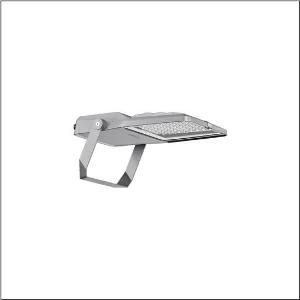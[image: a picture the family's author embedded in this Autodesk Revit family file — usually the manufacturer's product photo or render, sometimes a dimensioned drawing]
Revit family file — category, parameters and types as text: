
# Revit family: floodlight_fl_21_iq_mini___pl64_5xa7771c4e1a_d4bc
name_source: partatom
category: Lighting Fixtures
units: mm (PartAtom-declared; Revit-internal decimal feet)

## family parameters
Cut with Voids When Loaded = No
Host = Face
Light Source = No
Part Type = Normal
Room Calculation Point = No
Round Connector Dimension = Use Diameter
Shared = No

## types (1)
- --- (1 x LED, 12280 lm, 87.2 W, 4000K)
    Apparent Load = 87 VA
    CIE Flux Codes = 28 80 98 100 100
    Color Rendering = 70
    Color Temperature = 4000K
    Default Elevation = 1800 mm
    Description = Floodlight FL 21 iQ mini, floodlight, primary light control with lens, of PMMA, primary optical cover: protective disc, of toughened safety glass, transparent, light distribution: PL64, light emission: direct distribution, installation type: surface-mounted, lamps: LED, High Power LED, rated values: 12.280lm | 87,2W | 140,8lm/W (begin service life); end service life: 12.280lm | 92,1W; at 50% lumin. flux: 6.140lm | 40,2W | 152,7lm/W, colour temperature: 4000K, colour rendering: CRI > 70, light colour: 740, light setting 1 begin service life: 100% | 12.280lm | 87,2W | 140,8lm/W | 4.000K, light setting 1 end service life: 92,1W, further light settings possible, control: Auto-Match, Temp-Guard, Lumen-Switch, Night-Set, Smart-Wire, Light-Fading, Desk-Remote (wireless, voltage-free reading and setting of iQ features in the workshop via application-optimized NFC function/RFID function), optimised constant luminous flux control (CLO 2.0), pre-setting: linear dimming characteristic, with terminal, 6-pole, mains connection: 220..240V, AC, 50/60Hz, luminaire housing, of diecast aluminium, powder-coated, SITECO metallic grey (DB 702S), corrosivity category C5 mid according to DIN EN ISO 12944suitable for swimming poolschlorine-resistant, sealing non-destructively replaceable, mounting bracket, of steel, galvanised, powder-coated, SITECO metallic grey (DB 702S), protection rating (complete): IP66, insulation class (complete): insulation class II (safety insulation), certification: CE, ENEC, VDE, protection symbol: D, impact resistance: IK08, permissible operating ambient temperature: -40..+40°C, permissible operating ambient temperature for outdoor applications: -40..+50°C, standard: DIN EN 12944, LABS conformity tested according to VDMA 24364:2018-05, packaging unit: 1 piece

Light Distribution: PL64
    Height = 70 mm
    Lamp = 1 x LED
    Lamp Light Flux = 12280 lm
    Lamp Power = 87.2 W
    Lamp count = 1
    Length = 485 mm
    Luminous efficacy = 141 lm/W
    Manufacturer = Siteco
    ModVariant = No
    Model = 5XA7771C4E1A
    Mounting Place = Pole
    Mounting Type = Pole annexe
    Number of Poles = 1
    OnlyDefault = Yes
    Power Factor = 1
    Product Name = Floodlight FL 21 iQ mini | PL64
    Product group = floodlight | pylon annexe
    ProductGroupID = 6201
    Protection Class = Protection class II
    Protection Degree = IP 66
    RLX_Detail_Level = 1
    RLX_Emergency_Light_Flux = 0 lm
    RLX_Emergency_Type = 0
    RLX_Emergency_Type_DB = No
    RlxData = <blob elided: 96553 chars, md5=430a4146>
    Socket = socket
    Standby Power = 0 W
    System Light Flux = 12280 lm
    System Power = 87 W
    Type Comments = factory setting: luminous flux: 100 % | dim-lin: 254 | 456 mA
    Type Image = l_1006845.jpg
    URL = http://relux.com
    VarID = @adj_167611
    Voltage = 0 V
    Weight = 0.00 kg
    Width = 337 mm

## geometry (parser evidence)
native form markers: Blend x4, Sweep x13
no freeform markers — native parametric forms only
